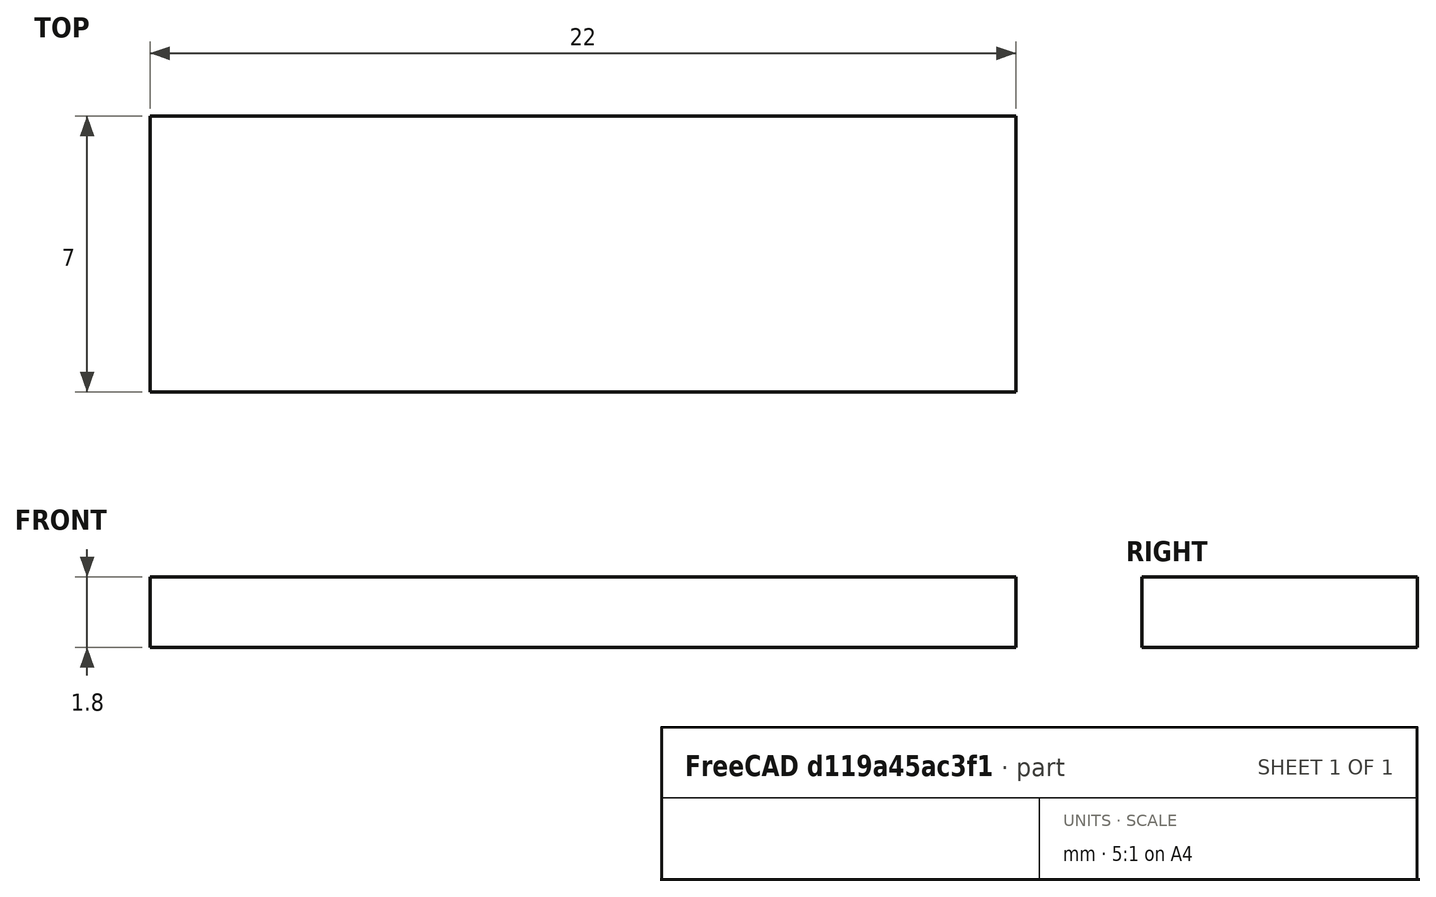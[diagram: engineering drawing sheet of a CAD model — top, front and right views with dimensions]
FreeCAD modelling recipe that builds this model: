
FCSTD DOCUMENT  (FreeCAD 0.16R6706 (Git))
Label: KXOB22-12X1F
License: All rights reserved
LicenseURL: http://en.wikipedia.org/wiki/All_rights_reserved
objects: Sketcher::SketchObject×1, PartDesign::Pad×1
note: 3 computed .brp shape members not serialized (recipe doc carries the construction recipe); baked Part::Feature solids carry a one-line shape summary decoded from their .brp

FEATURE [Sketcher::SketchObject] Sketch
  sketch-geometry (4):
    g0: LineSegment StartX=-11 StartY=3.5 StartZ=0 EndX=11 EndY=3.5 EndZ=0
    g1: LineSegment StartX=11 StartY=3.5 StartZ=0 EndX=11 EndY=-3.5 EndZ=0
    g2: LineSegment StartX=11 StartY=-3.5 StartZ=0 EndX=-11 EndY=-3.5 EndZ=0
    g3: LineSegment StartX=-11 StartY=-3.5 StartZ=0 EndX=-11 EndY=3.5 EndZ=0
  constraints (13):
    c: Coincident(g0,g1)
    c: Coincident(g1,g2)
    c: Coincident(g2,g3)
    c: Coincident(g3,g0)
    c: Perpendicular(g0,g3)
    c: Perpendicular(g1,g2)
    c: Equal(g1,g3)
    c: Equal(g0,g2)
    c: DistanceX(g0,g-1) = 11
    c: DistanceX(g-1,g1) = 11
    c: DistanceY(g2,g-1) = 3.5
    c: Parallel(g-2,g3)
    c: DistanceY(g3,g3) = 7
FEATURE [PartDesign::Pad] Pad
  Length = 1.8
  Length2 = 100
  Sketch = -> Sketch
  Type = 0
